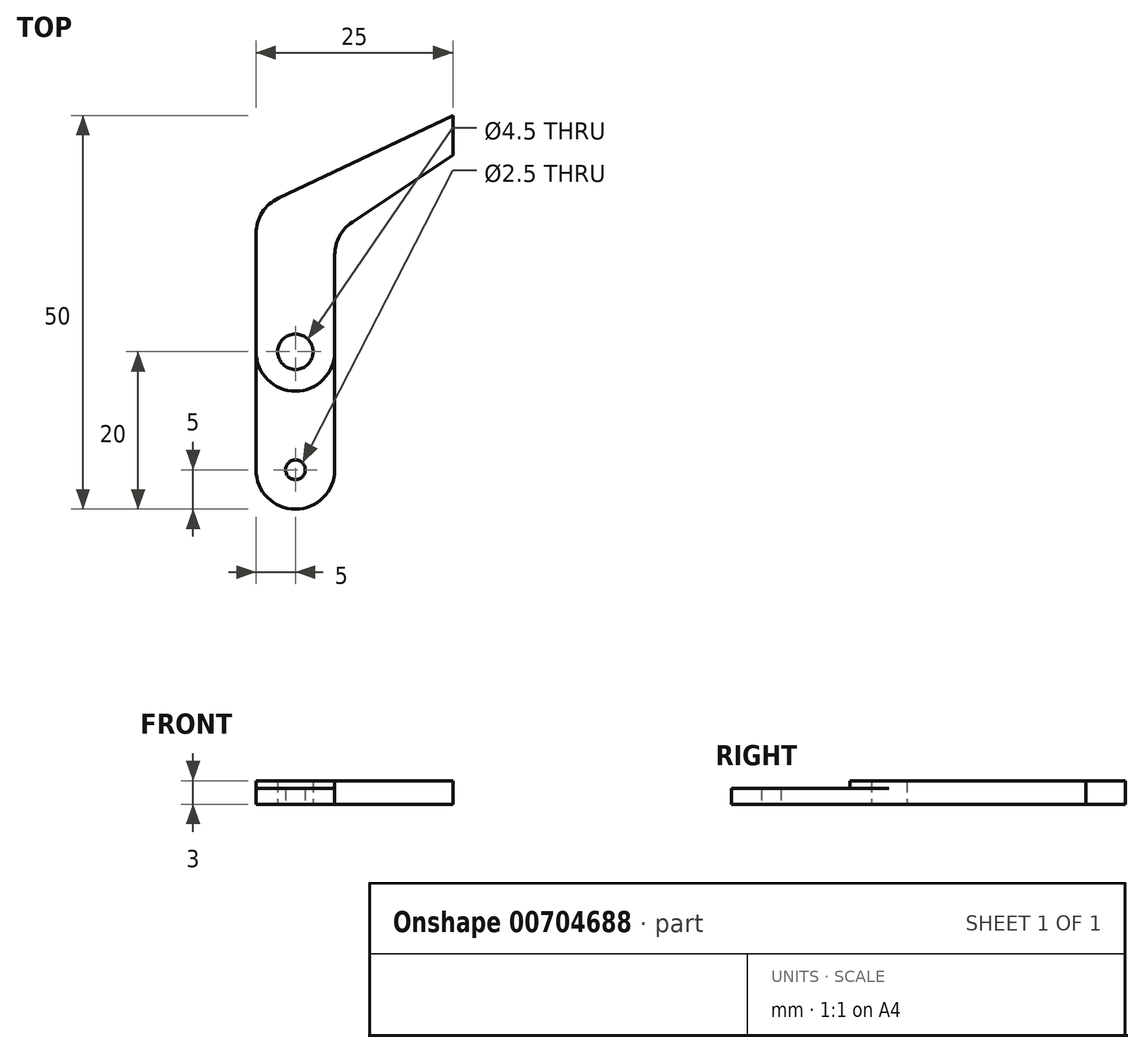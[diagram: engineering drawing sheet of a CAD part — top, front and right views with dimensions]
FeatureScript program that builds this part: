
annotation { "Feature Type Name" : "Feature", "Feature Type Description" : "" }
export const myFeature = defineFeature(function(context is Context, id is Id, definition is map)
    precondition{}
    {
        {
            var Q0;
            Q0=qCreatedBy(makeId("Top.planeOp"),FACE);
            var sketch = newSketch(context, id + "F0", { "sketchPlane" : qUnion([Q0])});
            skCircle(sketch, "E0", {"center": v(0, 0) * mm, "radius": 2.25 * mm});
            skCircle(sketch, "E1", {"center": v(0, 0) * mm, "radius": 5 * mm});
            skCircle(sketch, "E2", {"center": v(0, -15) * mm, "radius": 1.25 * mm});
            skCircle(sketch, "E3", {"center": v(0, -15) * mm, "radius": 5 * mm});
            skCircle(sketch, "E4", {"center": v(0, 15) * mm, "radius": 5 * mm});
            skLineSegment(sketch, "E5", {"start": v(-5, 15) * mm, "end": v(-5, 0) * mm});
            skLineSegment(sketch, "E6", {"start": v(-5, 0) * mm, "end": v(-5, -15) * mm});
            skLineSegment(sketch, "E7", {"start": v(5, 15) * mm, "end": v(5, 0) * mm});
            skLineSegment(sketch, "E8", {"start": v(5, 0) * mm, "end": v(5, -15) * mm});
            skLineSegment(sketch, "E9", {"start": v(-2.14, 19.52) * mm, "end": v(20, 30) * mm});
            skLineSegment(sketch, "E10", {"start": v(20, 30) * mm, "end": v(20, 25) * mm});
            skLineSegment(sketch, "E11", {"start": v(20, 25) * mm, "end": v(5, 15) * mm});
            skSolve(sketch);
        }
        {
            var Q0;
            Q0=makeQuery(id+"F0.imprint","IMPRINT",FACE,{"disambiguationData":[TD([[makeQuery(id+"F0.imprint","IMPRINT",EDGE,{"derivedFrom":sQuery(id+"F0.wireOp",EDGE,"E0")}),-1.0]])]});
            var Q1;
            {var subQ0=sQuery(id+"F0.wireOp",EDGE,"E5");Q1=makeQuery(id+"F0.imprint","IMPRINT",FACE,{"disambiguationData":[TD([[makeQuery(id+"F0.imprint","IMPRINT",EDGE,{"derivedFrom":subQ0}),1.0]])]});}
            var Q2;
            {var subQ0=sQuery(id+"F0.wireOp",EDGE,"E4");var subQ3=makeQuery(id+"F0.imprint","INTERSECT",VERTEX,{"derivedFrom":[subQ0,sQuery(id+"F0.wireOp",EDGE,"E5")]});Q2=makeQuery(id+"F0.imprint","IMPRINT",FACE,{"disambiguationData":[TD([[makeQuery(id+"F0.imprint","IMPRINT",EDGE,{"disambiguationData":[TD([[subQ3,1.0]])],"derivedFrom":subQ0}),1.0]])]});}
            var Q3;
            {var subQ2=sQuery(id+"F0.wireOp",EDGE,"E9");Q3=makeQuery(id+"F0.imprint","IMPRINT",FACE,{"disambiguationData":[TD([[makeQuery(id+"F0.imprint","IMPRINT",EDGE,{"derivedFrom":subQ2}),-1.0]])]});}
            extrude(context, id + "F1", {"entities" : qUnion([Q0, Q1, Q2, Q3]), "depth" : 3 * mm, "offsetDistance" : 25 * mm});
        }
        {
            var Q0;
            {var subQ0=sQuery(id+"F0.wireOp",EDGE,"E6");Q0=makeQuery(id+"F0.imprint","IMPRINT",FACE,{"disambiguationData":[TD([[makeQuery(id+"F0.imprint","IMPRINT",EDGE,{"derivedFrom":subQ0}),1.0]])]});}
            var Q1;
            Q1=makeQuery(id+"F0.imprint","IMPRINT",FACE,{"disambiguationData":[TD([[makeQuery(id+"F0.imprint","IMPRINT",EDGE,{"derivedFrom":sQuery(id+"F0.wireOp",EDGE,"E2")}),-1.0]])]});
            extrude(context, id + "F2", {"entities" : qUnion([Q0, Q1]), "operationType" : NewBodyOperationType.ADD, "depth" : 2 * mm, "offsetDistance" : 25 * mm});
        }
        {
            var Q0;
            Q0=makeQuery(id+"F1.opExtrude","SWEPT_EDGE",EDGE,{"disambiguationData":[OSD([sQuery(id+"F0.wireOp",EDGE,"E4"),sQuery(id+"F0.wireOp",EDGE,"E7"),sQuery(id+"F0.wireOp",EDGE,"E11")])]});
            fillet(context, id + "F3", {"entities" : qUnion([Q0]), "radius" : 5 * mm, "tangentPropagation" : true, "allowEdgeOverflow" : false});
        }
    });
